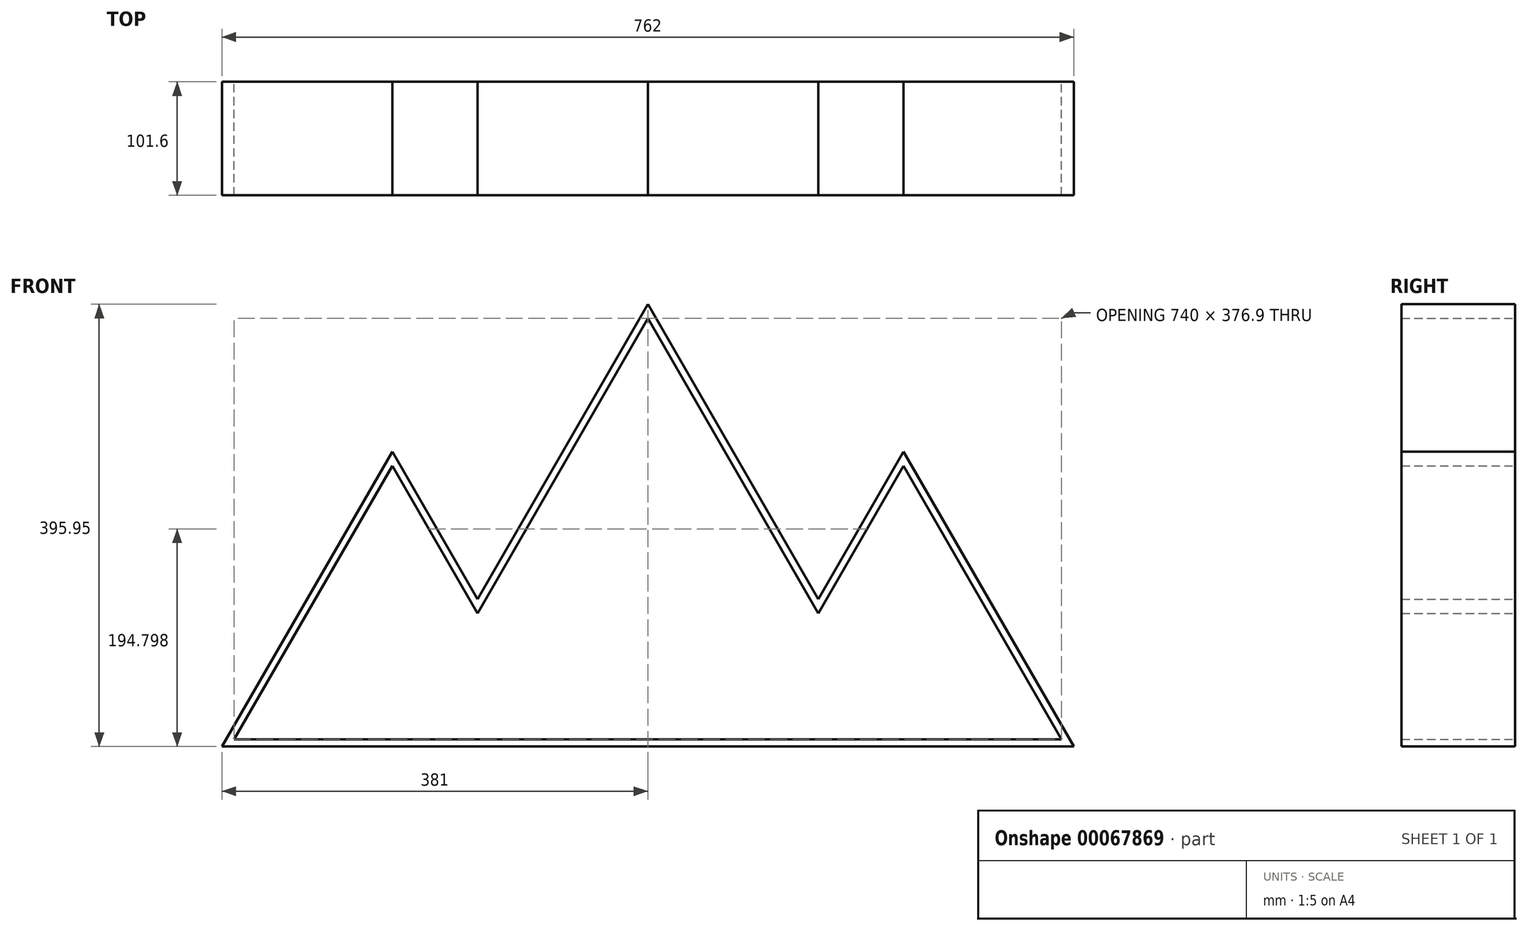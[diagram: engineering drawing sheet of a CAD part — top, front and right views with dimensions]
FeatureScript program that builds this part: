
annotation { "Feature Type Name" : "Feature", "Feature Type Description" : "" }
export const myFeature = defineFeature(function(context is Context, id is Id, definition is map)
    precondition{}
    {
        {
            var Q0;
            Q0=qCreatedBy(makeId("Front.planeOp"),FACE);
            var sketch = newSketch(context, id + "F0", { "sketchPlane" : qUnion([Q0])});
            skLineSegment(sketch, "E0", {"start": v(0, 0) * mm, "end": v(152.4, 263.96) * mm});
            skLineSegment(sketch, "E1", {"start": v(152.4, 263.96) * mm, "end": v(228.6, 131.98) * mm});
            skLineSegment(sketch, "E2", {"start": v(228.6, 131.98) * mm, "end": v(381, 395.95) * mm});
            skLineSegment(sketch, "E3", {"start": v(381, 395.95) * mm, "end": v(533.4, 131.98) * mm});
            skLineSegment(sketch, "E4", {"start": v(533.4, 131.98) * mm, "end": v(609.6, 263.96) * mm});
            skPoint(sketch, "E4.endSnap0", {"position": v(457.2, 263.96) * mm});
            skLineSegment(sketch, "E5", {"start": v(609.6, 263.96) * mm, "end": v(762, 0) * mm});
            skLineSegment(sketch, "E6", {"start": v(762, 0) * mm, "end": v(0, 0) * mm});
            skSolve(sketch);
        }
        {
            var Q0;
            Q0=makeQuery(id+"F0.imprint","IMPRINT",FACE,{"disambiguationData":[TD([[makeQuery(id+"F0.imprint","IMPRINT",EDGE,{"derivedFrom":sQuery(id+"F0.wireOp",EDGE,"E0")}),-1.0]])]});
            extrude(context, id + "F1", {"entities" : qUnion([Q0]), "depth" : 101.6 * mm});
        }
        {
            var Q0;
            Q0=makeQuery(id+"F1.opExtrude","CAP_FACE",FACE,{"disambiguationData":[OSD([sQuery(id+"F0.wireOp",EDGE,"E0"),sQuery(id+"F0.wireOp",EDGE,"E1"),sQuery(id+"F0.wireOp",EDGE,"E2"),sQuery(id+"F0.wireOp",EDGE,"E3"),sQuery(id+"F0.wireOp",EDGE,"E4"),sQuery(id+"F0.wireOp",EDGE,"E5"),sQuery(id+"F0.wireOp",EDGE,"E6")])],"isStart":false});
            shell(context, id + "F2", {"entities" : qUnion([Q0]), "thickness" : 6.35 * mm});
        }
        {
            var Q0;
            Q0=makeQuery(id+"F2.opShell","OFFSET_FACE",FACE,{"disambiguationData":[OSD([sQuery(id+"F0.wireOp",EDGE,"E0"),sQuery(id+"F0.wireOp",EDGE,"E1"),sQuery(id+"F0.wireOp",EDGE,"E2"),sQuery(id+"F0.wireOp",EDGE,"E3"),sQuery(id+"F0.wireOp",EDGE,"E4"),sQuery(id+"F0.wireOp",EDGE,"E5"),sQuery(id+"F0.wireOp",EDGE,"E6")])]});
            var sketch = newSketch(context, id + "F3", { "sketchPlane" : qUnion([Q0])});
            skLineSegment(sketch, "E7", {"start": v(11, 6.35) * mm, "end": v(152.4, 251.26) * mm});
            skLineSegment(sketch, "E8", {"start": v(152.4, 251.26) * mm, "end": v(228.6, 119.28) * mm});
            skLineSegment(sketch, "E9", {"start": v(228.6, 119.28) * mm, "end": v(381, 383.25) * mm});
            skLineSegment(sketch, "E10", {"start": v(381, 383.25) * mm, "end": v(533.4, 119.28) * mm});
            skLineSegment(sketch, "E11", {"start": v(533.4, 119.28) * mm, "end": v(609.6, 251.26) * mm});
            skLineSegment(sketch, "E12", {"start": v(609.6, 251.26) * mm, "end": v(751, 6.35) * mm});
            skLineSegment(sketch, "E13", {"start": v(751, 6.35) * mm, "end": v(11, 6.35) * mm});
            skSolve(sketch);
        }
        {
            var Q0;
            Q0=makeQuery(id+"F3.imprint","IMPRINT",FACE,{"disambiguationData":[TD([[makeQuery(id+"F3.imprint","IMPRINT",EDGE,{"derivedFrom":sQuery(id+"F3.wireOp",EDGE,"E7")}),-1.0]])]});
            extrude(context, id + "F4", {"entities" : qUnion([Q0]), "operationType" : NewBodyOperationType.REMOVE, "oppositeDirection" : true, "depth" : 6.35 * mm});
        }
    });
